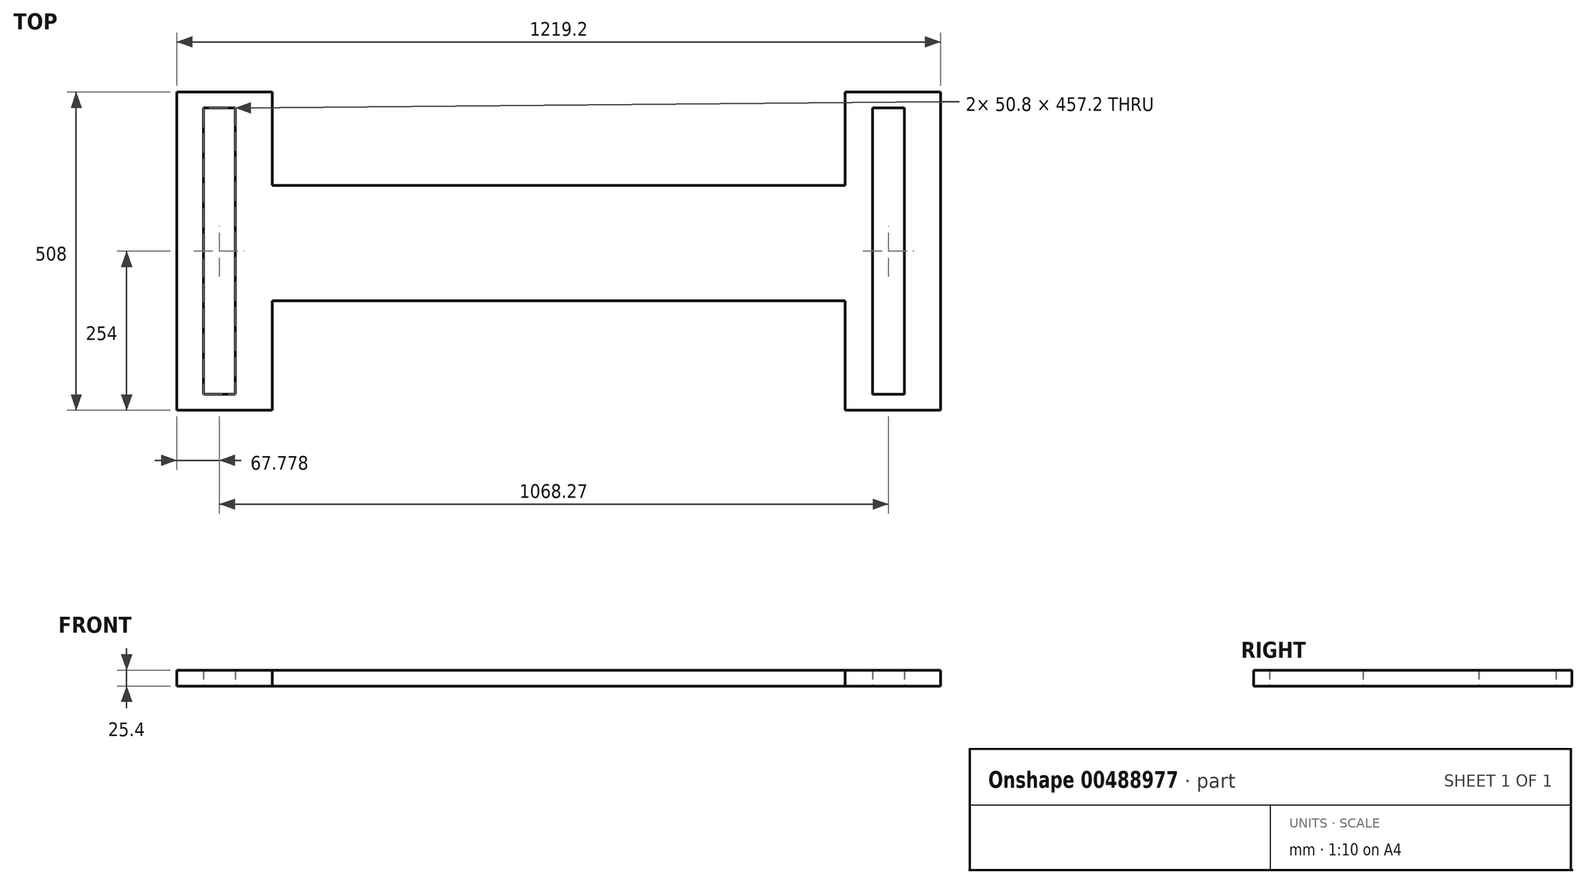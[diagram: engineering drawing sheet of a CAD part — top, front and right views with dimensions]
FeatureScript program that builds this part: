
annotation { "Feature Type Name" : "Feature", "Feature Type Description" : "" }
export const myFeature = defineFeature(function(context is Context, id is Id, definition is map)
    precondition{}
    {
        {
            var Q0;
            Q0=qCreatedBy(makeId("Top.planeOp"),FACE);
            var sketch = newSketch(context, id + "F0", { "sketchPlane" : qUnion([Q0])});
            skLineSegment(sketch, "E0", {"start": v(932.65, 482.6) * mm, "end": v(932.65, -25.4) * mm});
            skLineSegment(sketch, "E1", {"start": v(-286.55, -25.4) * mm, "end": v(-286.55, 482.6) * mm});
            skLineSegment(sketch, "E2.bottom", {"start": v(-244.17, 457.2) * mm, "end": v(-193.37, 457.2) * mm});
            skLineSegment(sketch, "E2.top", {"start": v(-244.17, 0) * mm, "end": v(-193.37, 0) * mm});
            skLineSegment(sketch, "E2.left", {"start": v(-244.17, 457.2) * mm, "end": v(-244.17, 0) * mm});
            skLineSegment(sketch, "E2.right", {"start": v(-193.37, 457.2) * mm, "end": v(-193.37, 0) * mm});
            skLineSegment(sketch, "E3", {"start": v(874.9, 457.2) * mm, "end": v(874.9, 0) * mm});
            skLineSegment(sketch, "E4", {"start": v(874.9, 0) * mm, "end": v(824.1, 0) * mm});
            skLineSegment(sketch, "E5", {"start": v(824.1, 0) * mm, "end": v(824.1, 457.2) * mm});
            skLineSegment(sketch, "E6", {"start": v(824.1, 457.2) * mm, "end": v(874.9, 457.2) * mm});
            skLineSegment(sketch, "E7", {"start": v(-286.55, 482.6) * mm, "end": v(-134.15, 482.6) * mm});
            skLineSegment(sketch, "E8", {"start": v(-134.15, 482.6) * mm, "end": v(-134.15, 333.44) * mm});
            skLineSegment(sketch, "E9", {"start": v(-134.15, 333.44) * mm, "end": v(780.25, 333.44) * mm});
            skLineSegment(sketch, "E10", {"start": v(780.25, 333.44) * mm, "end": v(780.25, 482.6) * mm});
            skLineSegment(sketch, "E11", {"start": v(780.25, 482.6) * mm, "end": v(932.65, 482.6) * mm});
            skLineSegment(sketch, "E12", {"start": v(-286.55, -25.4) * mm, "end": v(-134.15, -25.4) * mm});
            skLineSegment(sketch, "E13", {"start": v(-134.15, -25.4) * mm, "end": v(-134.15, 149.01) * mm});
            skLineSegment(sketch, "E14", {"start": v(-134.15, 149.01) * mm, "end": v(780.25, 149.01) * mm});
            skLineSegment(sketch, "E15", {"start": v(780.25, 149.01) * mm, "end": v(780.25, -25.4) * mm});
            skLineSegment(sketch, "E16", {"start": v(780.25, -25.4) * mm, "end": v(932.65, -25.4) * mm});
            skSolve(sketch);
        }
        {
            var Q0;
            Q0=makeQuery(id+"F0.imprint","IMPRINT",FACE,{"disambiguationData":[TD([[makeQuery(id+"F0.imprint","IMPRINT",EDGE,{"derivedFrom":sQuery(id+"F0.wireOp",EDGE,"E0")}),-1.0]])]});
            extrude(context, id + "F1", {"entities" : qUnion([Q0]), "depth" : 25.4 * mm, "offsetDistance" : 25.4 * mm});
        }
    });
